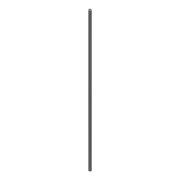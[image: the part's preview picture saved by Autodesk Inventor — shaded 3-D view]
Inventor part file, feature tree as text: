
AUTODESK INVENTOR PART (.ipt)
format: ipt  version: 2016 (Build 200138000, 138)  size: 92,672 bytes
history: native  units: mm
features: sketch x3, hole x2, extrude x1, chamfer x1, reference x1
ambient origin geometry x8: Origin, YZ Plane, XZ Plane, XY Plane, X Axis, Y Axis, Z Axis, Center Point
bodies: Solid1 (feature_tree)
feature tree (8):
  extrude  "Extrusion1"  Depth=533.0mm TaperAngle=0.0deg
  hole  "Hole1"  [1 undecoded]
  hole  "Hole2"  [1 undecoded]
  chamfer  "Chamfer1"  [1 undecoded]
  sketch  "Sketch1"  dims[d0=10.0mm d1=533.0mm d2=0.0mm]
  reference  "Reference1"
  sketch  "Sketch2"  dims[d3=3.242mm d4=12.0mm d5=4.0mm d6=2.0mm d7=90.0deg d8=17.0mm d9=20.594885mm]
  sketch  "Sketch3"  dims[d10=3.242mm d11=12.0mm d12=4.0mm d13=2.0mm d14=90.0deg d15=17.0mm d16=20.594885mm d17=0.2mm d18=2.0mm d19=45.0deg]
note: 3 required parameter values undecoded (feature->parameter linkage not recoverable at this tier; creation-order binding heuristic only, values carry confidence <= 0.55)
